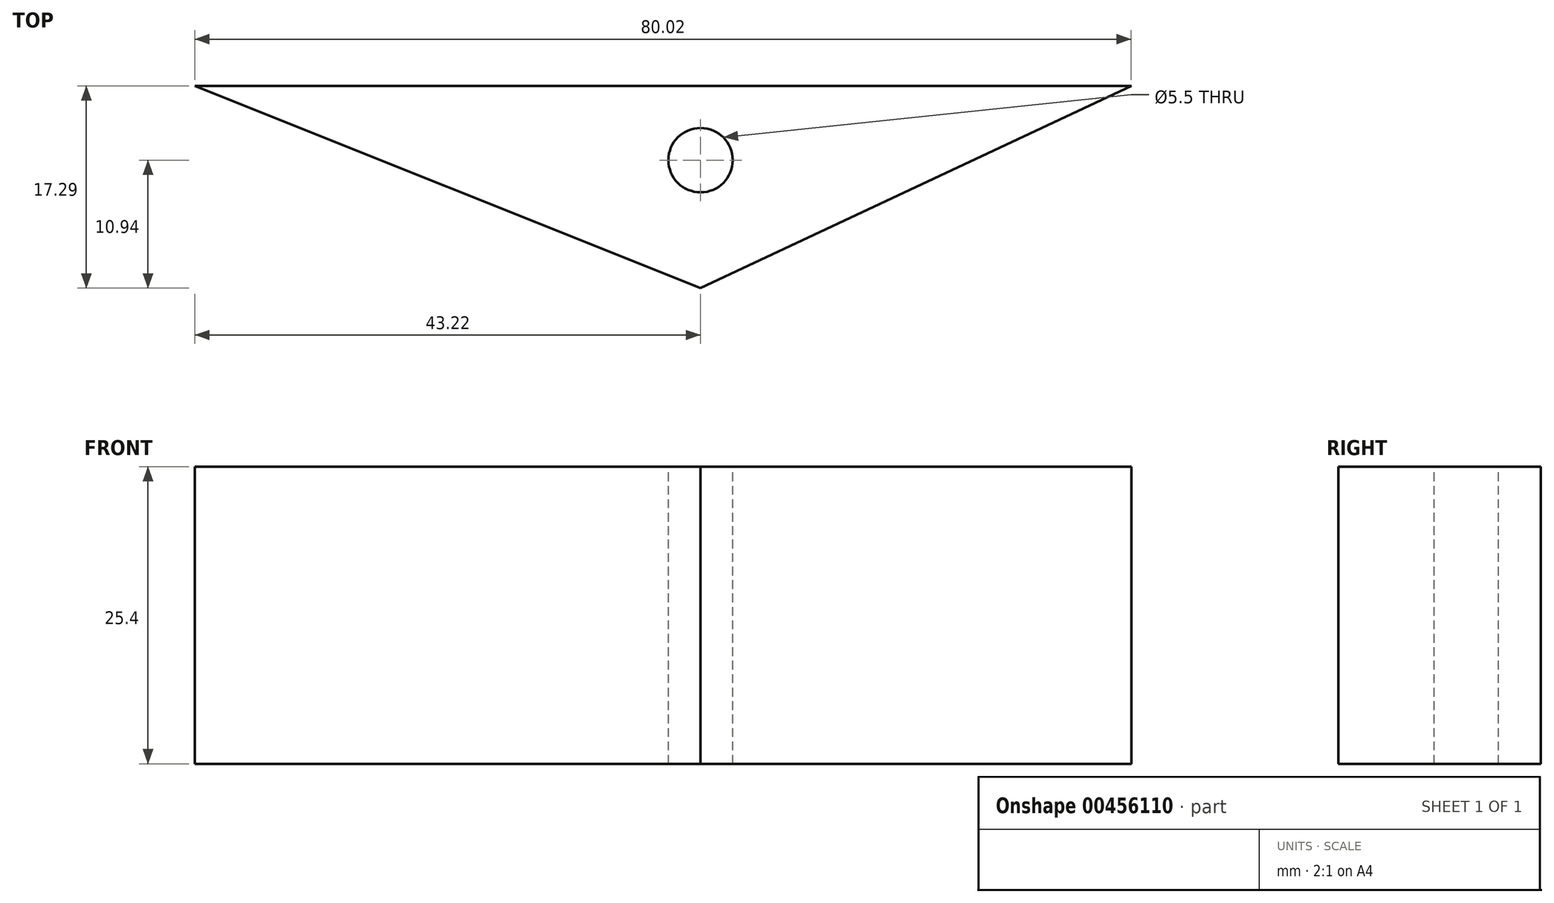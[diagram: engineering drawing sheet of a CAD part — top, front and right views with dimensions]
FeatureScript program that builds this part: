
annotation { "Feature Type Name" : "Feature", "Feature Type Description" : "" }
export const myFeature = defineFeature(function(context is Context, id is Id, definition is map)
    precondition{}
    {
        {
            var Q0;
            Q0=qCreatedBy(makeId("Top.planeOp"),FACE);
            var sketch = newSketch(context, id + "F0", { "sketchPlane" : qUnion([Q0])});
            skLineSegment(sketch, "E0", {"start": v(0, 0) * mm, "end": v(-43.22, 17.29) * mm});
            skLineSegment(sketch, "E1", {"start": v(-43.22, 17.29) * mm, "end": v(36.8, 17.29) * mm});
            skLineSegment(sketch, "E2", {"start": v(36.8, 17.29) * mm, "end": v(0, 0) * mm});
            skSolve(sketch);
        }
        {
            var Q0;
            Q0 = qSketchRegion(id + "F0", true);
            extrude(context, id + "F1", {"entities" : qUnion([Q0]), "depth" : 25.4 * mm});
        }
        {
            var Q0;
            Q0=makeQuery(id+"F1.opExtrude","CAP_FACE",FACE,{"disambiguationData":[OSD([sQuery(id+"F0.wireOp",EDGE,"E0"),sQuery(id+"F0.wireOp",EDGE,"E1"),sQuery(id+"F0.wireOp",EDGE,"E2")])],"isStart":false});
            var sketch = newSketch(context, id + "F2", { "sketchPlane" : qUnion([Q0])});
            skPoint(sketch, "E3", {"position": v(0, 10.94) * mm});
            skSolve(sketch);
        }
        {
            var Q0;
            Q0=sQuery(id+"F2.wireOp",VERTEX,"E3");
            var Q1;
            Q1=makeQuery(id+"F1.opExtrude","SWEPT_BODY",BODY,{"disambiguationData":[OSD([sQuery(id+"F0.wireOp",EDGE,"E0"),sQuery(id+"F0.wireOp",EDGE,"E1"),sQuery(id+"F0.wireOp",EDGE,"E2")])]});
            hole(context, id + "F3", {"style" : HoleStyle.SIMPLE, "endStyle" : HoleEndStyle.THROUGH, "holeDiameter" : 5.5 * mm, "isTappedThrough" : true, "tappedDepth" : 12.7 * mm, "tapClearance" : 3, "locations" : qUnion([Q0]), "scope" : qUnion([Q1])});
        }
    });
